# Revit family: Gira_543300
name_source: partatom
category: Electrical Fixtures
revit_build: Autodesk Revit 2017 (Build: 20160225_1515(x64)
units: mm (PartAtom-declared; Revit-internal decimal feet)

## family parameters
Cut with Voids When Loaded = No
Host = Face
Maintain Annotation Orientation = No
Part Type = Normal
Room Calculation Point = No
Round Connector Dimension = Use Diameter
Shared = No

## types (1)
- WL swit./m-c act. 1-g DRA Gira eNet
    App control via Bluetooth = No
    Applicable with button = No
    Applicable with infrared button = No
    Applicable with movement sensor = No
    Applicable with presence indicator = No
    Applicable with time switch/timer = No
    Applicable with transmission button = No
    BIM = https://media.live.bim.site X1 REG KNX.rfa
    BIMSITE_PRODUCT_ID = 09d5c4e62c6d905a1ec09bf9e37d86a6310b734c
    Bus connection included = No
    Cost = 0 $
    Default Elevation = 1219 mm
    Description = WL swit. m-c act.1g DRA eNet eNet wireless switching momentary-contact actuator, 1-gang,DRA Features: Can be set with eNet server:: - Fully encrypted wireless transmission (AES CCM) from eNet Server software version 2.0. - Operation locks. - Device software update. - The eNet wireless switching or wireless momentary-contact actuator receives telegrams for switching lighting from the eNet wireless reception module or eNet server via a data cable. - Operating modes: Switching actuator or momentary-contact actuator. - Status feedback to eNet wireless transmitter. - Scene operation. - Operating mode buttons: Relay contact stays closed as long as telegrams are being received (max. 60 seconds). Can be set with eNet server:: - Flashing function. - Delay time. - Switch-on off delay. - Switch-off pre-warning. - Minimum switching repeat time. - Permanent-on, permanent-off.,Notes : - An eNet wireless reception module or an eNet server is required to operate this DIN-rail mounting device.
    Dimming phase cut-off = No
    Dimming phase cut-on = No
    GTIN = 4010337774273
    HAN = 543300
    Halogen free = No
    HeinzeBIM = https://www.heinze.de
    Light value memory = No
    Local operation/hand operation = No
    Manufacturer = Gira
    Max. switching power [Voltampere] = 2300
    Modulare Erweiterungsmöglichkeit = No
    Number of binary inputs = 1
    Number of inputs = 0
    Number of outputs = 0
    Parallel-service possible = No
    Power boost suitable = No
    Radio frequent bidirectional = No
    Serial dimmer = No
    Suitable for C-load = No
    Transparent = No
    URL = https://www.gira.de
    Verschiedene Phasen anschließbar = No
    With label area = No

## geometry (parser evidence)
native form markers: Blend x2, Sweep x3
no freeform markers — native parametric forms only
